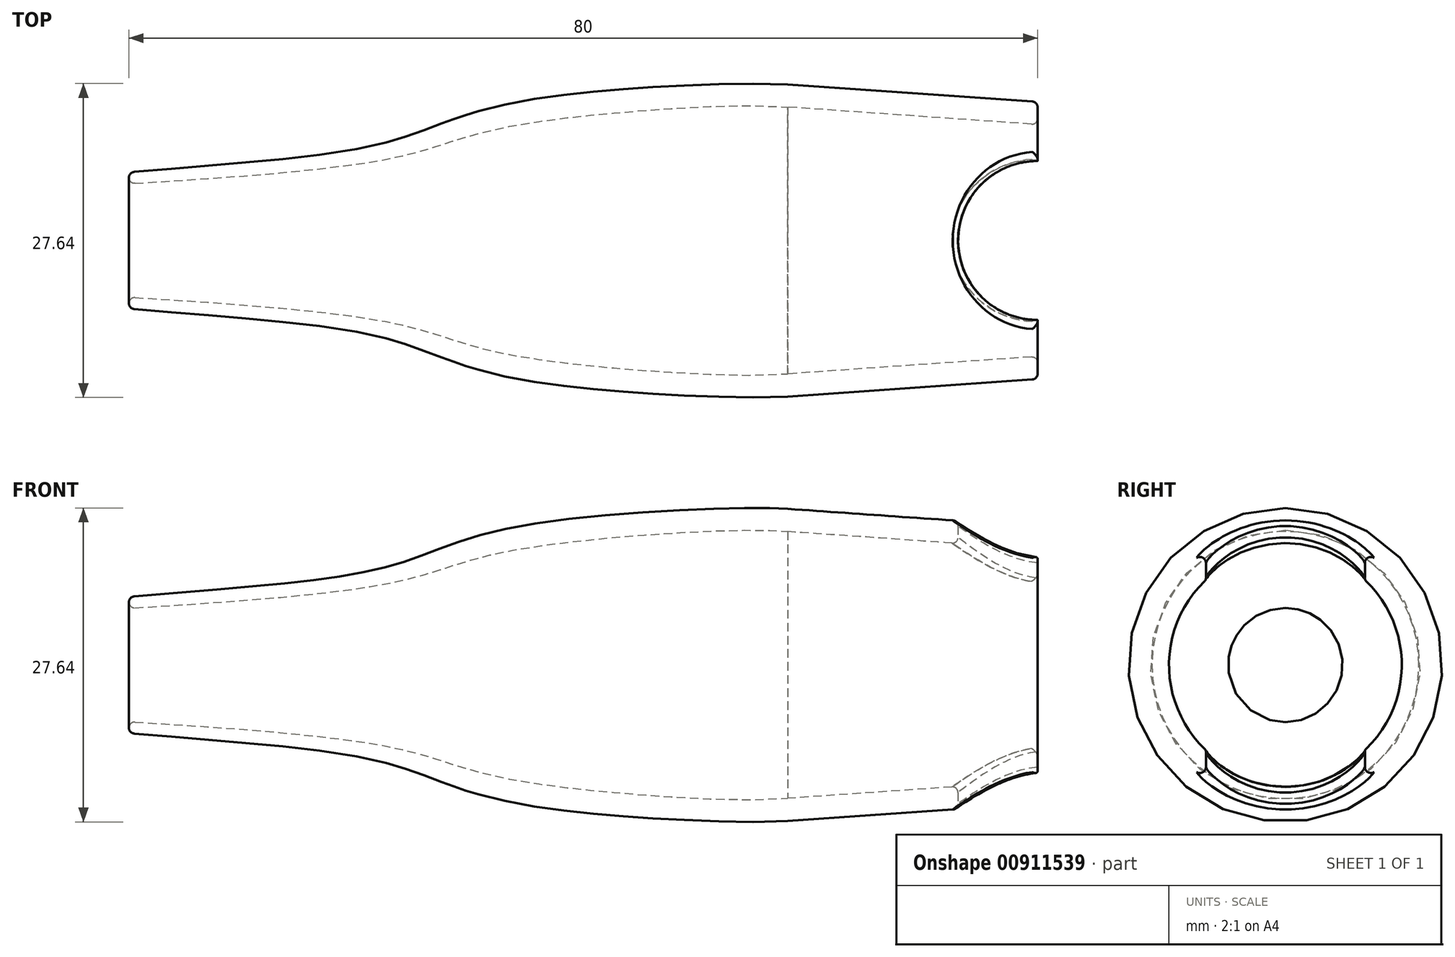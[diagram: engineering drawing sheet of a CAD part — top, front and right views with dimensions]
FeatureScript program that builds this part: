
annotation { "Feature Type Name" : "Feature", "Feature Type Description" : "" }
export const myFeature = defineFeature(function(context is Context, id is Id, definition is map)
    precondition{}
    {
        {
            var Q0;
            Q0=qCreatedBy(makeId("Front.planeOp"),FACE);
            var sketch = newSketch(context, id + "F0", { "sketchPlane" : qUnion([Q0])});
            skLineSegment(sketch, "E0", {"start": v(58, 13.75) * mm, "end": v(80, 12.21) * mm});
            skLineSegment(sketch, "E1", {"start": v(80, 12.21) * mm, "end": v(80, 10.21) * mm});
            skLineSegment(sketch, "E2", {"start": v(0, 6) * mm, "end": v(0, 5) * mm});
            skLineSegment(sketch, "E3", {"start": v(58, 11.75) * mm, "end": v(80, 10.21) * mm});
            skPoint(sketch, "E4.orphan", {"position": v(80, 0) * mm});
            skLineSegment(sketch, "E5", {"start": v(-2.44, 0) * mm, "end": v(52.34, 0) * mm, "construction": true});
            skFitSpline(sketch, "E6", {"points": [v(0, 6) * mm, v(23.18, 8.77) * mm, v(34.01, 12.16) * mm, v(58, 13.75) * mm], "startDerivative": vector(93.83, 8.05) * mm, "endDerivative": vector(28.53, -2) * mm});
            skFitSpline(sketch, "E7", {"points": [v(0, 5) * mm, v(26.19, 8) * mm, v(34.5, 10.23) * mm, v(58, 11.75) * mm], "startDerivative": vector(124.96, 7.45) * mm, "endDerivative": vector(28.59, -3.58) * mm});
            skSolve(sketch);
        }
        {
            var Q0;
            Q0=qSketchRegion(id+"F0",true);
            var Q1;
            Q1=sQuery(id+"F0.wireOp",EDGE,"E5");
            revolve(context, id + "F1", {"surfaceOperationType" : NewSurfaceOperationType.NEW, "entities" : qUnion([Q0]), "axis" : qUnion([Q1]), "revolveType" : RevolveType.FULL});
        }
        {
            var Q0;
            Q0=qCreatedBy(makeId("Top.planeOp"),FACE);
            var sketch = newSketch(context, id + "F2", { "sketchPlane" : qUnion([Q0])});
            skLineSegment(sketch, "E8.0", {"start": v(80, -12.21) * mm, "end": v(80, 12.21) * mm, "construction": true});
            skLineSegment(sketch, "E9", {"start": v(-8.08, 0) * mm, "end": v(63.94, 0) * mm, "construction": true});
            skArc(sketch, "E10", {"start": v(80, 7) * mm, "mid": v(73, 0) * mm, "end": v(80, -7) * mm});
            skLineSegment(sketch, "E11", {"start": v(80, 7) * mm, "end": v(80, -7) * mm});
            skSolve(sketch);
        }
        {
            var Q0;
            Q0 = qSketchRegion(id + "F2", true);
            extrude(context, id + "F3", {"entities" : qUnion([Q0]), "operationType" : NewBodyOperationType.REMOVE, "endBound" : BoundingType.SYMMETRIC, "depth" : 30 * mm, "offsetDistance" : 25 * mm});
        }
        {
            var Q0;
            Q0=makeQuery(id+"F3.boolean.opBoolean","INTERSECT",EDGE,{"disambiguationData":[OD(1.0)],"derivedFrom":[makeQuery(id+"F1.opRevolve","SWEPT_FACE",FACE,{"disambiguationData":[OSD([sQuery(id+"F0.wireOp",EDGE,"E0")])]}),makeQuery(id+"F3.opExtrude","SWEPT_FACE",FACE,{"disambiguationData":[OSD([sQuery(id+"F2.wireOp",EDGE,"E10")])]})]});
            var Q1;
            Q1=makeQuery(id+"F3.boolean.opBoolean","INTERSECT",EDGE,{"disambiguationData":[OD(1.0)],"derivedFrom":[makeQuery(id+"F1.opRevolve","SWEPT_FACE",FACE,{"disambiguationData":[OSD([sQuery(id+"F0.wireOp",EDGE,"E3")])]}),makeQuery(id+"F3.opExtrude","SWEPT_FACE",FACE,{"disambiguationData":[OSD([sQuery(id+"F2.wireOp",EDGE,"E10")])]})]});
            var Q2;
            Q2=makeQuery(id+"F3.boolean.opBoolean","INTERSECT",EDGE,{"disambiguationData":[OD(0.0)],"derivedFrom":[makeQuery(id+"F1.opRevolve","SWEPT_FACE",FACE,{"disambiguationData":[OSD([sQuery(id+"F0.wireOp",EDGE,"E0")])]}),makeQuery(id+"F3.opExtrude","SWEPT_FACE",FACE,{"disambiguationData":[OSD([sQuery(id+"F2.wireOp",EDGE,"E10")])]})]});
            var Q3;
            Q3=makeQuery(id+"F3.boolean.opBoolean","INTERSECT",EDGE,{"disambiguationData":[OD(0.0)],"derivedFrom":[makeQuery(id+"F1.opRevolve","SWEPT_FACE",FACE,{"disambiguationData":[OSD([sQuery(id+"F0.wireOp",EDGE,"E3")])]}),makeQuery(id+"F3.opExtrude","SWEPT_FACE",FACE,{"disambiguationData":[OSD([sQuery(id+"F2.wireOp",EDGE,"E10")])]})]});
            var Q4;
            Q4=makeQuery(id+"F3.boolean.opBoolean","SPLIT",EDGE,{"disambiguationData":[OD(0.0)],"derivedFrom":makeQuery(id+"F1.opRevolve","SWEPT_EDGE",EDGE,{"disambiguationData":[OSD([sQuery(id+"F0.wireOp",EDGE,"E0"),sQuery(id+"F0.wireOp",EDGE,"E1")])]})});
            var Q5;
            Q5=makeQuery(id+"F3.boolean.opBoolean","SPLIT",EDGE,{"disambiguationData":[OD(0.0)],"derivedFrom":makeQuery(id+"F1.opRevolve","SWEPT_EDGE",EDGE,{"disambiguationData":[OSD([sQuery(id+"F0.wireOp",EDGE,"E1"),sQuery(id+"F0.wireOp",EDGE,"E3")])]})});
            var Q6;
            Q6=makeQuery(id+"F3.boolean.opBoolean","SPLIT",EDGE,{"disambiguationData":[OD(1.0)],"derivedFrom":makeQuery(id+"F1.opRevolve","SWEPT_EDGE",EDGE,{"disambiguationData":[OSD([sQuery(id+"F0.wireOp",EDGE,"E1"),sQuery(id+"F0.wireOp",EDGE,"E3")])]})});
            var Q7;
            Q7=makeQuery(id+"F3.boolean.opBoolean","SPLIT",EDGE,{"disambiguationData":[OD(1.0)],"derivedFrom":makeQuery(id+"F1.opRevolve","SWEPT_EDGE",EDGE,{"disambiguationData":[OSD([sQuery(id+"F0.wireOp",EDGE,"E0"),sQuery(id+"F0.wireOp",EDGE,"E1")])]})});
            var Q8;
            Q8=makeQuery(id+"F1.opRevolve","SWEPT_EDGE",EDGE,{"disambiguationData":[OSD([sQuery(id+"F0.wireOp",EDGE,"E2"),sQuery(id+"F0.wireOp",EDGE,"E6")])]});
            var Q9;
            Q9=makeQuery(id+"F1.opRevolve","SWEPT_EDGE",EDGE,{"disambiguationData":[OSD([sQuery(id+"F0.wireOp",EDGE,"E2"),sQuery(id+"F0.wireOp",EDGE,"E7")])]});
            fillet(context, id + "F4", {"entities" : qUnion([Q0, Q1, Q2, Q3, Q4, Q5, Q6, Q7, Q8, Q9]), "radius" : 0.5 * mm, "tangentPropagation" : true, "allowEdgeOverflow" : false});
        }
    });
